# Revit family: Faucet-Lavatory-KOHLER-Singulier-K-10861AR
name_source: partatom
category: Plumbing Fixtures
revit_build: Autodesk Revit 2017 (Build: 20160225_1515(x64)
units: mm (PartAtom-declared; Revit-internal decimal feet)

## family parameters
Cut with Voids When Loaded = No
Host = Face
OmniClass Number = 23.31.11.00
OmniClass Title = Faucets
Part Type = Normal
Room Calculation Point = No
Round Connector Dimension = Use Diameter
Shared = No

## types (3) — shared parameters
ADA Compliant = No
Assembly Code = D2010
CW Connection = Yes
Cold Water Inlet = Cold Water Inlet
Date Modified = 07/27/2020
Default Elevation = 36"
Description = Tall single-hole bathroom sink faucet
Flow Rate = 0 GPM
HW Connection = Yes
Handle Clearance = 3 5/16"
Height = 13"
Hot Water Inlet = Hot Water Inlet
Length = 5 1/8"
Manufacturer = KOHLER Co.
Master Format 2014 = 22 41 39
Master Format 2014 Name = Residential Faucets, Supplies, and Trim
Material = Metal Consturction
Pressure = 0.00 psi
Product Name = Singulier
Spout Reach = 5 1/8"
URL = https://la.kohler.com
Vent Connection = No
Waste Connection = No
Waste Water Outlet = Waste Water Outlet
WaterSense Certified = No
Width = 1 7/8"

## per-type parameters (varying)
| type | Drain Included | Finish | Model | Type |
| CP- Polished Chrome | Yes | Kohler-Metal-CP-Polished_Chrome | K-10861AR-4-CP | 1 |
| Without Drain, CP-Polished Chrome | No | Kohler-Metal-CP-Polished_Chrome | K-10861AR-4ND-CP | 3 |
| Without Drain,AF- French Gold | No | Kohler-Metal-AF-Vibrant_French_Gold | K-10861AR-4ND-AF | 2 |

## geometry (parser evidence)
native form markers: Sweep x6
no freeform markers — native parametric forms only
